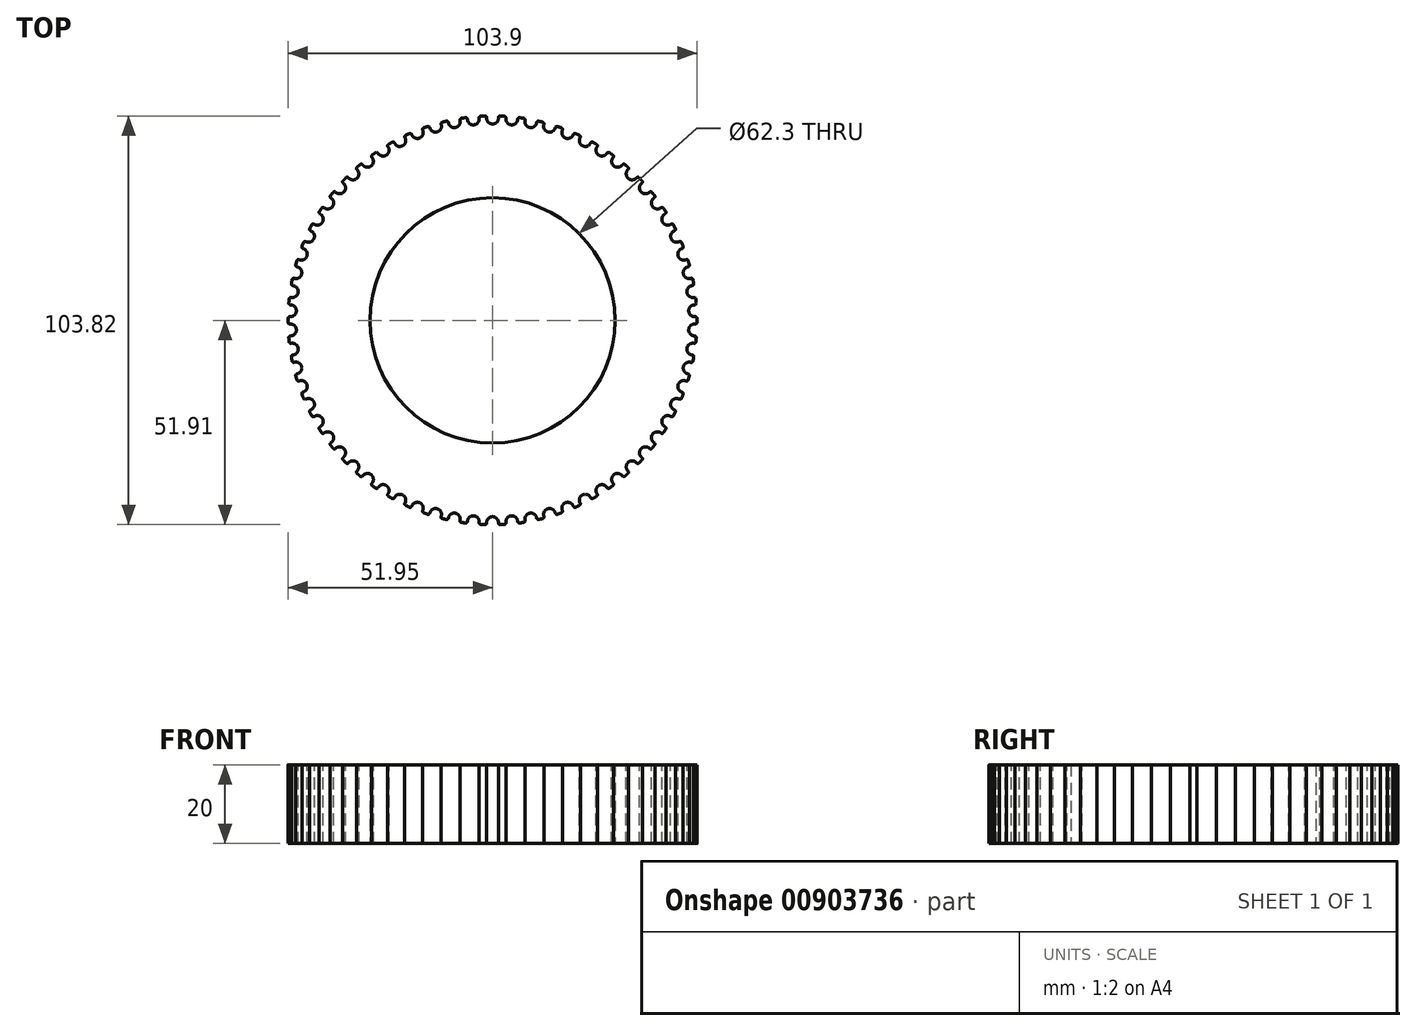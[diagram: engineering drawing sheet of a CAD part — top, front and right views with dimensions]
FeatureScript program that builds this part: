
annotation { "Feature Type Name" : "Feature", "Feature Type Description" : "" }
export const myFeature = defineFeature(function(context is Context, id is Id, definition is map)
    precondition{}
    {
        {
            assignVariable(context, id + "F0", {"name" : "Teeth", "anyValue" : 66});
        }
        {
            assignVariable(context, id + "F1", {"name" : "Width", "anyValue" : 20});
        }
        {
            var Q0;
            Q0=qCreatedBy(makeId("Top.planeOp"),FACE);
            var sketch = newSketch(context, id + "F2", { "sketchPlane" : qUnion([Q0])});
            skCircle(sketch, "E0", {"center": v(0, 0) * mm, "radius": 51.95 * mm});
            skSolve(sketch);
        }
        {
            var Q0;
            Q0=qSketchRegion(id+"F2",true);
            extrude(context, id + "F3", {"entities" : qUnion([Q0]), "depth" : (getVariable(context, 'Width')) * mm});
        }
        {
            var Q0;
            Q0=makeQuery(id+"F3.opExtrude","CAP_FACE",FACE,{"disambiguationData":[OSD([sQuery(id+"F2.wireOp",EDGE,"E0")])],"isStart":false});
            var sketch = newSketch(context, id + "F4", { "sketchPlane" : qUnion([Q0])});
            skCircle(sketch, "E1", {"center": v(0, 0) * mm, "radius": 49.89 * mm, "construction": true});
            skArc(sketch, "E2", {"start": v(-1.5, 51.44) * mm, "mid": v(0, 49.89) * mm, "end": v(1.5, 51.44) * mm});
            skArc(sketch, "E3", {"start": v(1.97, 51.91) * mm, "mid": v(0, 51.95) * mm, "end": v(-1.97, 51.91) * mm});
            skArc(sketch, "E4", {"start": v(-1.5, 51.44) * mm, "mid": v(-1.63, 51.78) * mm, "end": v(-1.97, 51.91) * mm});
            skArc(sketch, "E5", {"start": v(1.97, 51.91) * mm, "mid": v(1.63, 51.78) * mm, "end": v(1.5, 51.44) * mm});
            skSolve(sketch);
        }
        {
            var Q0;
            Q0=makeQuery(id+"F4.imprint","IMPRINT",FACE,{"disambiguationData":[TD([[makeQuery(id+"F4.imprint","IMPRINT",EDGE,{"derivedFrom":sQuery(id+"F4.wireOp",EDGE,"E2")}),1.0]])]});
            var Q1;
            Q1=makeQuery(id+"F3.opExtrude","CAP_FACE",FACE,{"disambiguationData":[OSD([sQuery(id+"F2.wireOp",EDGE,"E0")])],"isStart":true});
            extrude(context, id + "F5", {"entities" : qUnion([Q0]), "operationType" : NewBodyOperationType.REMOVE, "endBound" : BoundingType.UP_TO_SURFACE, "oppositeDirection" : true, "endBoundEntityFace" : qUnion([Q1]), "depth" : 25 * mm, "offsetDistance" : 25 * mm});
        }
        {
            var Q0;
            Q0=makeQuery(id+"F5.boolean.opBoolean","COPY",FACE,{"derivedFrom":makeQuery(id+"F5.opExtrude","SWEPT_FACE",FACE,{"disambiguationData":[OSD([sQuery(id+"F4.wireOp",EDGE,"E4")])]})});
            var Q1;
            Q1=makeQuery(id+"F5.boolean.opBoolean","COPY",FACE,{"derivedFrom":makeQuery(id+"F5.opExtrude","SWEPT_FACE",FACE,{"disambiguationData":[OSD([sQuery(id+"F4.wireOp",EDGE,"kHu0Iwj9-o4Cv-DRlk-4OjM-lw9Y4UkXsprA")])]})});
            var Q2;
            Q2=makeQuery(id+"F5.boolean.opBoolean","COPY",FACE,{"derivedFrom":makeQuery(id+"F5.opExtrude","SWEPT_FACE",FACE,{"disambiguationData":[OSD([sQuery(id+"F4.wireOp",EDGE,"E2")])]})});
            var Q3;
            Q3=makeQuery(id+"F5.boolean.opBoolean","COPY",FACE,{"derivedFrom":makeQuery(id+"F5.opExtrude","SWEPT_FACE",FACE,{"disambiguationData":[OSD([sQuery(id+"F4.wireOp",EDGE,"lCBZwTSR-BtAH-iuKv-YoZ4-wjcx4KIexOll")])]})});
            var Q4;
            Q4=makeQuery(id+"F5.boolean.opBoolean","COPY",FACE,{"derivedFrom":makeQuery(id+"F5.opExtrude","SWEPT_FACE",FACE,{"disambiguationData":[OSD([sQuery(id+"F4.wireOp",EDGE,"E5")])]})});
            var Q5;
            Q5=makeQuery(id+"F3.opExtrude","SWEPT_FACE",FACE,{"disambiguationData":[OSD([sQuery(id+"F2.wireOp",EDGE,"E0")])]});
            circularPattern(context, id + "F6", {"faces" : qUnion([Q0, Q1, Q2, Q3, Q4]), "axis" : qUnion([Q5]), "angle" : 360 * degree, "instanceCount" : getVariable(context, 'Teeth'), "equalSpace" : true, "patternType" : PatternType.FACE});
        }
        {
            var Q0;
            Q0=makeQuery(id+"F3.opExtrude","CAP_FACE",FACE,{"disambiguationData":[OSD([sQuery(id+"F2.wireOp",EDGE,"E0")])],"isStart":true});
            var sketch = newSketch(context, id + "F7", { "sketchPlane" : qUnion([Q0])});
            skCircle(sketch, "E6", {"center": v(0, 0) * mm, "radius": 31.15 * mm});
            skSolve(sketch);
        }
        {
            var Q0;
            Q0 = qSketchRegion(id + "F7", true);
            extrude(context, id + "F8", {"entities" : qUnion([Q0]), "operationType" : NewBodyOperationType.REMOVE, "oppositeDirection" : true, "depth" : 25 * mm, "offsetDistance" : 25 * mm});
        }
    });
